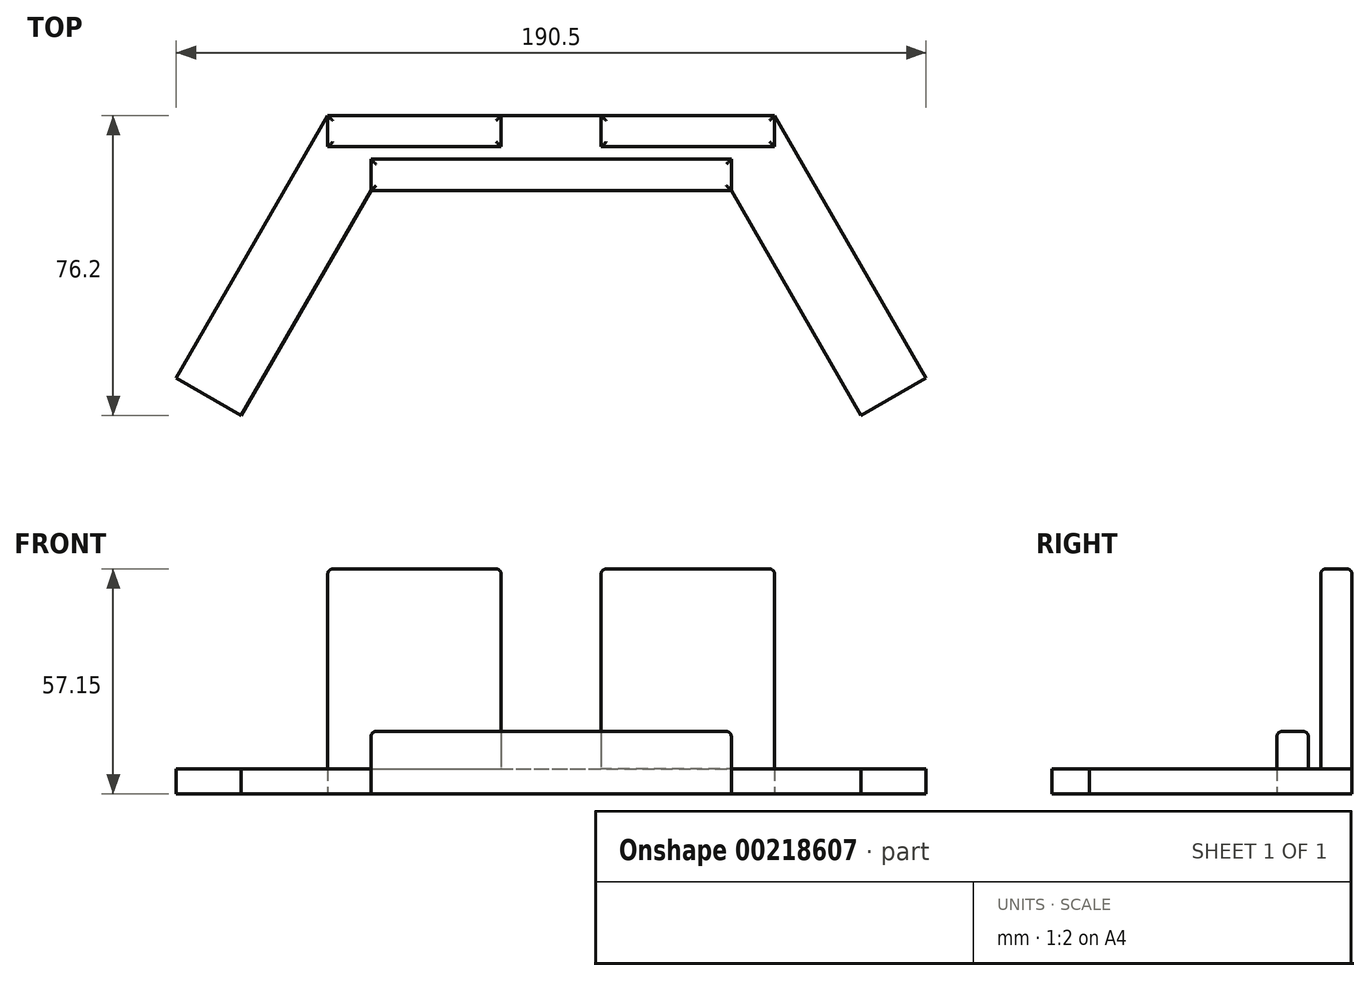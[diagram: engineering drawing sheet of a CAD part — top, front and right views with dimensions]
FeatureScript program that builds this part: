
annotation { "Feature Type Name" : "Feature", "Feature Type Description" : "" }
export const myFeature = defineFeature(function(context is Context, id is Id, definition is map)
    precondition{}
    {
        {
            var Q0;
            Q0=qCreatedBy(makeId("Top.planeOp"),FACE);
            var sketch = newSketch(context, id + "F0", { "sketchPlane" : qUnion([Q0])});
            skLineSegment(sketch, "E0", {"start": v(-56.76, 0) * mm, "end": v(56.76, 0) * mm});
            skLineSegment(sketch, "E1", {"start": v(-56.76, 0) * mm, "end": v(-95.25, -66.68) * mm});
            skLineSegment(sketch, "E2", {"start": v(-95.25, -66.68) * mm, "end": v(-78.75, -76.2) * mm});
            skLineSegment(sketch, "E3", {"start": v(-78.75, -76.2) * mm, "end": v(-45.76, -19.05) * mm});
            skLineSegment(sketch, "E4", {"start": v(-45.76, -19.05) * mm, "end": v(0, -19.05) * mm});
            skLineSegment(sketch, "E5.MirrorCS", {"start": v(45.76, -19.05) * mm, "end": v(0, -19.05) * mm});
            skLineSegment(sketch, "E6.MirrorCS", {"start": v(78.75, -76.2) * mm, "end": v(45.76, -19.05) * mm});
            skLineSegment(sketch, "E7.MirrorCS", {"start": v(95.25, -66.68) * mm, "end": v(78.75, -76.2) * mm});
            skLineSegment(sketch, "E8.MirrorCS", {"start": v(56.76, 0) * mm, "end": v(95.25, -66.68) * mm});
            skSolve(sketch);
        }
        {
            var Q0;
            Q0 = qSketchRegion(id + "F0", true);
            extrude(context, id + "F1", {"entities" : qUnion([Q0]), "depth" : 6.35 * mm, "offsetDistance" : 25.4 * mm});
        }
        {
            var Q0;
            Q0=makeQuery(id+"F1.opExtrude","CAP_FACE",FACE,{"disambiguationData":[OSD([sQuery(id+"F0.wireOp",EDGE,"E0"),sQuery(id+"F0.wireOp",EDGE,"E1"),sQuery(id+"F0.wireOp",EDGE,"E2"),sQuery(id+"F0.wireOp",EDGE,"E3"),sQuery(id+"F0.wireOp",EDGE,"E4"),sQuery(id+"F0.wireOp",EDGE,"E5.MirrorCS"),sQuery(id+"F0.wireOp",EDGE,"E6.MirrorCS"),sQuery(id+"F0.wireOp",EDGE,"E7.MirrorCS"),sQuery(id+"F0.wireOp",EDGE,"E8.MirrorCS")])],"isStart":false});
            var sketch = newSketch(context, id + "F2", { "sketchPlane" : qUnion([Q0])});
            skLineSegment(sketch, "E9.bottom", {"start": v(-56.76, 0) * mm, "end": v(-12.7, 0) * mm});
            skLineSegment(sketch, "E9.top", {"start": v(-56.76, -7.94) * mm, "end": v(-12.7, -7.94) * mm});
            skLineSegment(sketch, "E9.left", {"start": v(-56.76, 0) * mm, "end": v(-56.76, -7.94) * mm});
            skLineSegment(sketch, "E9.right", {"start": v(-12.7, 0) * mm, "end": v(-12.7, -7.94) * mm});
            skLineSegment(sketch, "E10", {"start": v(0, 0) * mm, "end": v(0, -19.05) * mm, "construction": true});
            skLineSegment(sketch, "E11", {"start": v(0, -9.53) * mm, "end": v(32.33, -9.53) * mm, "construction": true});
            skLineSegment(sketch, "E12.MirrorCS", {"start": v(56.76, 0) * mm, "end": v(12.7, 0) * mm});
            skLineSegment(sketch, "E13.MirrorCS", {"start": v(12.7, 0) * mm, "end": v(12.7, -7.94) * mm});
            skLineSegment(sketch, "E14.MirrorCS", {"start": v(56.76, -7.94) * mm, "end": v(12.7, -7.94) * mm});
            skLineSegment(sketch, "E15.MirrorCS", {"start": v(56.76, 0) * mm, "end": v(56.76, -7.94) * mm});
            skSolve(sketch);
        }
        {
            var Q0;
            Q0 = qSketchRegion(id + "F2", true);
            extrude(context, id + "F3", {"entities" : qUnion([Q0]), "operationType" : NewBodyOperationType.ADD, "depth" : 50.8 * mm, "offsetDistance" : 25.4 * mm});
        }
        {
            var Q0;
            Q0=makeQuery(id+"F1.opExtrude","CAP_FACE",FACE,{"disambiguationData":[OSD([sQuery(id+"F0.wireOp",EDGE,"E0"),sQuery(id+"F0.wireOp",EDGE,"E1"),sQuery(id+"F0.wireOp",EDGE,"E2"),sQuery(id+"F0.wireOp",EDGE,"E3"),sQuery(id+"F0.wireOp",EDGE,"E4"),sQuery(id+"F0.wireOp",EDGE,"E5.MirrorCS"),sQuery(id+"F0.wireOp",EDGE,"E6.MirrorCS"),sQuery(id+"F0.wireOp",EDGE,"E7.MirrorCS"),sQuery(id+"F0.wireOp",EDGE,"E8.MirrorCS")])],"isStart":false});
            var sketch = newSketch(context, id + "F4", { "sketchPlane" : qUnion([Q0])});
            skLineSegment(sketch, "E16.bottom", {"start": v(-45.76, -19.05) * mm, "end": v(45.76, -19.05) * mm});
            skLineSegment(sketch, "E16.top", {"start": v(-45.76, -11.11) * mm, "end": v(45.76, -11.11) * mm});
            skLineSegment(sketch, "E16.left", {"start": v(-45.76, -19.05) * mm, "end": v(-45.76, -11.11) * mm});
            skLineSegment(sketch, "E16.right", {"start": v(45.76, -19.05) * mm, "end": v(45.76, -11.11) * mm});
            skSolve(sketch);
        }
        {
            var Q0;
            Q0 = qSketchRegion(id + "F4", true);
            extrude(context, id + "F5", {"entities" : qUnion([Q0]), "operationType" : NewBodyOperationType.ADD, "depth" : 9.52 * mm, "offsetDistance" : 25.4 * mm});
        }
        {
            var Q0;
            Q0=makeQuery(id+"F5.opExtrude","CAP_FACE",FACE,{"disambiguationData":[OSD([sQuery(id+"F4.wireOp",EDGE,"E16.bottom"),sQuery(id+"F4.wireOp",EDGE,"E16.top"),sQuery(id+"F4.wireOp",EDGE,"E16.left"),sQuery(id+"F4.wireOp",EDGE,"E16.right")])],"isStart":false});
            var Q1;
            Q1=makeQuery(id+"F3.opExtrude","CAP_FACE",FACE,{"disambiguationData":[OSD([sQuery(id+"F2.wireOp",EDGE,"E9.bottom"),sQuery(id+"F2.wireOp",EDGE,"E9.top"),sQuery(id+"F2.wireOp",EDGE,"E9.left"),sQuery(id+"F2.wireOp",EDGE,"E9.right")])],"isStart":false});
            var Q2;
            Q2=makeQuery(id+"F3.opExtrude","CAP_FACE",FACE,{"disambiguationData":[OSD([sQuery(id+"F2.wireOp",EDGE,"E12.MirrorCS"),sQuery(id+"F2.wireOp",EDGE,"E13.MirrorCS"),sQuery(id+"F2.wireOp",EDGE,"E14.MirrorCS"),sQuery(id+"F2.wireOp",EDGE,"E15.MirrorCS")])],"isStart":false});
            var Q3;
            Q3=makeQuery(id+"F3.opExtrude","CAP_EDGE",EDGE,{"disambiguationData":[OSD([sQuery(id+"F2.wireOp",EDGE,"E9.left")])],"isStart":true});
            var Q4;
            Q4=makeQuery(id+"F3.opExtrude","CAP_EDGE",EDGE,{"disambiguationData":[OSD([sQuery(id+"F2.wireOp",EDGE,"E9.top")])],"isStart":true});
            var Q5;
            Q5=makeQuery(id+"F5.opExtrude","CAP_EDGE",EDGE,{"disambiguationData":[OSD([sQuery(id+"F4.wireOp",EDGE,"E16.left")])],"isStart":true});
            var Q6;
            Q6=makeQuery(id+"F5.opExtrude","CAP_EDGE",EDGE,{"disambiguationData":[OSD([sQuery(id+"F4.wireOp",EDGE,"E16.top")])],"isStart":true});
            var Q7;
            Q7=makeQuery(id+"F3.opExtrude","CAP_EDGE",EDGE,{"disambiguationData":[OSD([sQuery(id+"F2.wireOp",EDGE,"E14.MirrorCS")])],"isStart":true});
            var Q8;
            Q8=makeQuery(id+"F5.opExtrude","CAP_EDGE",EDGE,{"disambiguationData":[OSD([sQuery(id+"F4.wireOp",EDGE,"E16.right")])],"isStart":true});
            var Q9;
            Q9=makeQuery(id+"F3.opExtrude","CAP_EDGE",EDGE,{"disambiguationData":[OSD([sQuery(id+"F2.wireOp",EDGE,"E15.MirrorCS")])],"isStart":true});
            fillet(context, id + "F6", {"entities" : qUnion([Q0, Q1, Q2, Q3, Q4, Q5, Q6, Q7, Q8, Q9]), "tangentPropagation" : true, "radius" : 1.27 * mm, "defaultsChanged" : false, "vertexSettings" : [], "allowEdgeOverflow" : false});
        }
    });
